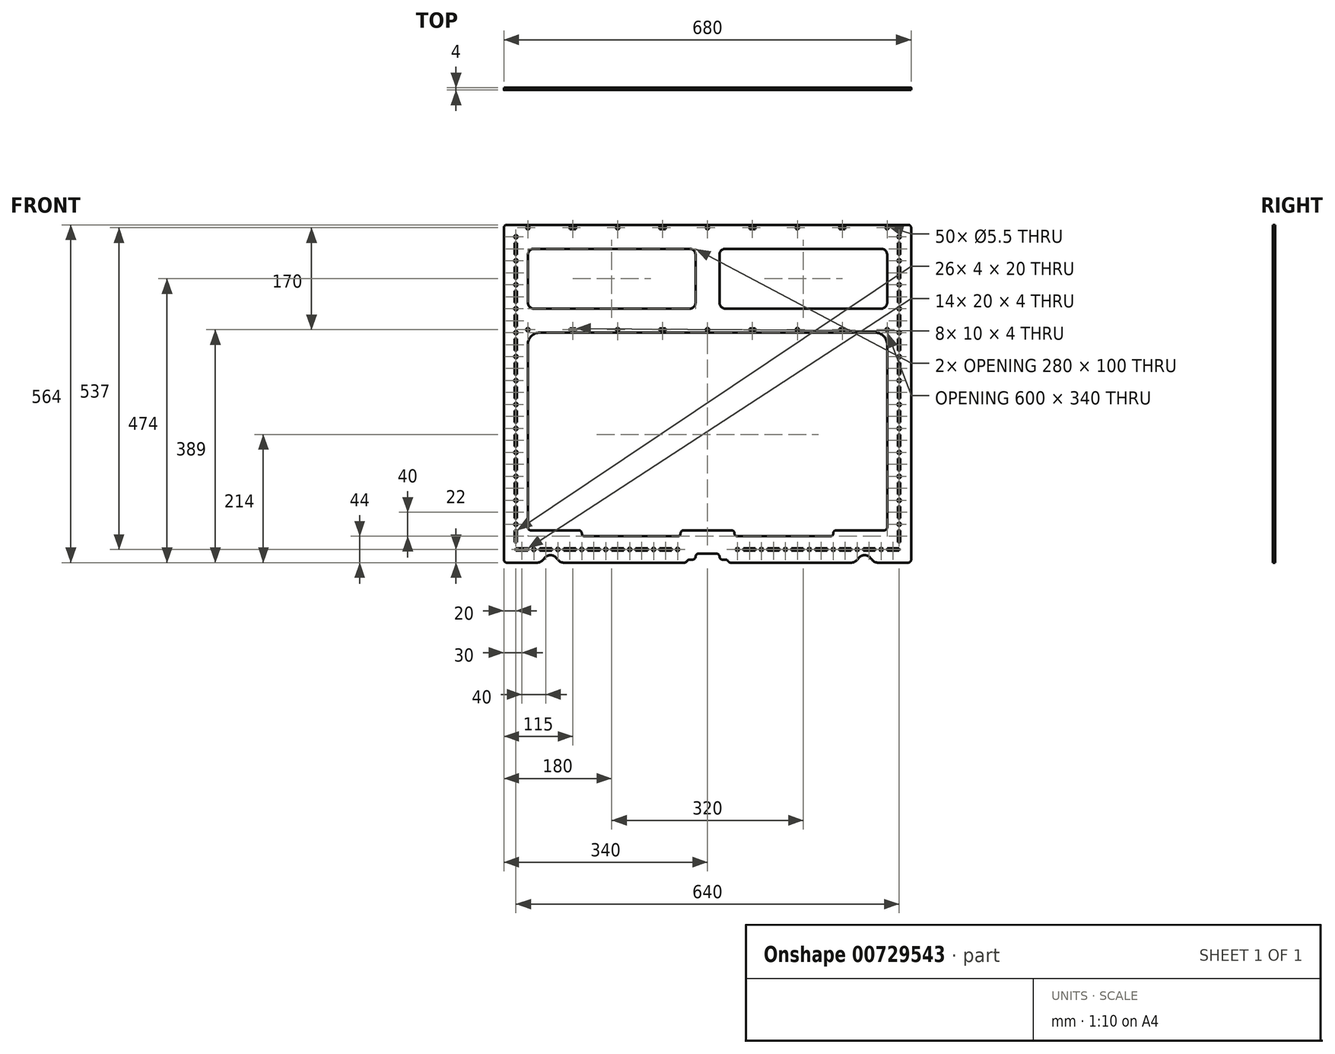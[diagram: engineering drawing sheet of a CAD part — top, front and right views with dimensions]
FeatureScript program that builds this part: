
annotation { "Feature Type Name" : "Feature", "Feature Type Description" : "" }
export const myFeature = defineFeature(function(context is Context, id is Id, definition is map)
    precondition{}
    {
        {
            var Q0;
            Q0=qCreatedBy(makeId("Front.planeOp"),FACE);
            var sketch = newSketch(context, id + "F0", { "sketchPlane" : qUnion([Q0])});
            skLineSegment(sketch, "E0.bottom", {"start": v(0, 0) * mm, "end": v(640, 0) * mm, "construction": true});
            skLineSegment(sketch, "E0.top", {"start": v(0, 365) * mm, "end": v(640, 365) * mm, "construction": true});
            skLineSegment(sketch, "E0.left", {"start": v(0, 0) * mm, "end": v(0, 540) * mm, "construction": true});
            skLineSegment(sketch, "E0.right", {"start": v(640, 0) * mm, "end": v(640, 540) * mm, "construction": true});
            skLineSegment(sketch, "E1.top", {"start": v(-15, -24) * mm, "end": v(34.7, -24) * mm});
            skLineSegment(sketch, "E2.bottom", {"start": v(40, 360) * mm, "end": v(600, 360) * mm});
            skLineSegment(sketch, "E2.top", {"start": v(115, 20) * mm, "end": v(270, 20) * mm});
            skLineSegment(sketch, "E2.left", {"start": v(20, 340) * mm, "end": v(20, 35) * mm});
            skLineSegment(sketch, "E2.right", {"start": v(620, 340) * mm, "end": v(620, 35) * mm});
            skLineSegment(sketch, "E3.top", {"start": v(-15, 540) * mm, "end": v(655, 540) * mm});
            skLineSegment(sketch, "E4.bottom", {"start": v(30, 500) * mm, "end": v(290, 500) * mm});
            skLineSegment(sketch, "E4.top", {"start": v(30, 400) * mm, "end": v(290, 400) * mm});
            skLineSegment(sketch, "E4.left", {"start": v(20, 490) * mm, "end": v(20, 410) * mm});
            skLineSegment(sketch, "E4.right", {"start": v(620, 490) * mm, "end": v(620, 410) * mm});
            skLineSegment(sketch, "E5", {"start": v(0, 535) * mm, "end": v(640, 535) * mm, "construction": true});
            skLineSegment(sketch, "E6", {"start": v(660, 535) * mm, "end": v(660, -19) * mm});
            skLineSegment(sketch, "E7", {"start": v(-20, 535) * mm, "end": v(-20, -19) * mm});
            skCircle(sketch, "E8", {"center": v(20, 535) * mm, "radius": 2.75 * mm});
            skLineSegment(sketch, "E9.bottom", {"start": v(0, 0) * mm, "end": v(20, 0) * mm});
            skLineSegment(sketch, "E9.top", {"start": v(0, -4) * mm, "end": v(20, -4) * mm});
            skLineSegment(sketch, "E9.left", {"start": v(0, 0) * mm, "end": v(0, -4) * mm});
            skLineSegment(sketch, "E9.right", {"start": v(20, 0) * mm, "end": v(20, -4) * mm});
            skLineSegment(sketch, "E10.bottom", {"start": v(2, 10) * mm, "end": v(-2, 10) * mm});
            skLineSegment(sketch, "E10.top", {"start": v(2, 30) * mm, "end": v(-2, 30) * mm});
            skLineSegment(sketch, "E10.left", {"start": v(2, 10) * mm, "end": v(2, 30) * mm});
            skLineSegment(sketch, "E10.right", {"start": v(-2, 10) * mm, "end": v(-2, 30) * mm});
            skPoint(sketch, "E10.middle", {"position": v(0, 20) * mm});
            skCircle(sketch, "E11.1.0.0", {"center": v(170, 535) * mm, "radius": 2.75 * mm});
            skCircle(sketch, "E11.2.0.0", {"center": v(320, 535) * mm, "radius": 2.75 * mm});
            skCircle(sketch, "E11.3.0.0", {"center": v(470, 535) * mm, "radius": 2.75 * mm});
            skCircle(sketch, "E11.4.0.0", {"center": v(620, 535) * mm, "radius": 2.75 * mm});
            skLineSegment(sketch, "E11.direction1", {"start": v(20, 535) * mm, "end": v(170, 535) * mm, "construction": true});
            skCircle(sketch, "E12", {"center": v(20, 365) * mm, "radius": 2.75 * mm});
            skCircle(sketch, "E13.1.0.0", {"center": v(170, 365) * mm, "radius": 2.75 * mm});
            skCircle(sketch, "E13.2.0.0", {"center": v(320, 365) * mm, "radius": 2.75 * mm});
            skCircle(sketch, "E13.3.0.0", {"center": v(470, 365) * mm, "radius": 2.75 * mm});
            skCircle(sketch, "E13.4.0.0", {"center": v(620, 365) * mm, "radius": 2.75 * mm});
            skLineSegment(sketch, "E13.direction1", {"start": v(20, 365) * mm, "end": v(170, 365) * mm, "construction": true});
            skCircle(sketch, "E14", {"center": v(0, 40) * mm, "radius": 2.75 * mm});
            skLineSegment(sketch, "E15.0.1.0", {"start": v(2, 50) * mm, "end": v(-2, 50) * mm});
            skLineSegment(sketch, "E15.0.1.1", {"start": v(-2, 50) * mm, "end": v(-2, 70) * mm});
            skLineSegment(sketch, "E15.0.1.2", {"start": v(2, 50) * mm, "end": v(2, 70) * mm});
            skLineSegment(sketch, "E15.0.1.3", {"start": v(2, 70) * mm, "end": v(-2, 70) * mm});
            skCircle(sketch, "E15.0.1.4", {"center": v(0, 80) * mm, "radius": 2.75 * mm});
            skLineSegment(sketch, "E15.0.2.0", {"start": v(2, 90) * mm, "end": v(-2, 90) * mm});
            skLineSegment(sketch, "E15.0.2.1", {"start": v(-2, 90) * mm, "end": v(-2, 110) * mm});
            skLineSegment(sketch, "E15.0.2.2", {"start": v(2, 90) * mm, "end": v(2, 110) * mm});
            skLineSegment(sketch, "E15.0.2.3", {"start": v(2, 110) * mm, "end": v(-2, 110) * mm});
            skCircle(sketch, "E15.0.2.4", {"center": v(0, 120) * mm, "radius": 2.75 * mm});
            skLineSegment(sketch, "E15.0.3.0", {"start": v(2, 130) * mm, "end": v(-2, 130) * mm});
            skLineSegment(sketch, "E15.0.3.1", {"start": v(-2, 130) * mm, "end": v(-2, 150) * mm});
            skLineSegment(sketch, "E15.0.3.2", {"start": v(2, 130) * mm, "end": v(2, 150) * mm});
            skLineSegment(sketch, "E15.0.3.3", {"start": v(2, 150) * mm, "end": v(-2, 150) * mm});
            skCircle(sketch, "E15.0.3.4", {"center": v(0, 160) * mm, "radius": 2.75 * mm});
            skLineSegment(sketch, "E15.0.4.0", {"start": v(2, 170) * mm, "end": v(-2, 170) * mm});
            skLineSegment(sketch, "E15.0.4.1", {"start": v(-2, 170) * mm, "end": v(-2, 190) * mm});
            skLineSegment(sketch, "E15.0.4.2", {"start": v(2, 170) * mm, "end": v(2, 190) * mm});
            skLineSegment(sketch, "E15.0.4.3", {"start": v(2, 190) * mm, "end": v(-2, 190) * mm});
            skCircle(sketch, "E15.0.4.4", {"center": v(0, 200) * mm, "radius": 2.75 * mm});
            skLineSegment(sketch, "E15.0.5.0", {"start": v(2, 210) * mm, "end": v(-2, 210) * mm});
            skLineSegment(sketch, "E15.0.5.1", {"start": v(-2, 210) * mm, "end": v(-2, 230) * mm});
            skLineSegment(sketch, "E15.0.5.2", {"start": v(2, 210) * mm, "end": v(2, 230) * mm});
            skLineSegment(sketch, "E15.0.5.3", {"start": v(2, 230) * mm, "end": v(-2, 230) * mm});
            skCircle(sketch, "E15.0.5.4", {"center": v(0, 240) * mm, "radius": 2.75 * mm});
            skLineSegment(sketch, "E15.0.6.0", {"start": v(2, 250) * mm, "end": v(-2, 250) * mm});
            skLineSegment(sketch, "E15.0.6.1", {"start": v(-2, 250) * mm, "end": v(-2, 270) * mm});
            skLineSegment(sketch, "E15.0.6.2", {"start": v(2, 250) * mm, "end": v(2, 270) * mm});
            skLineSegment(sketch, "E15.0.6.3", {"start": v(2, 270) * mm, "end": v(-2, 270) * mm});
            skCircle(sketch, "E15.0.6.4", {"center": v(0, 280) * mm, "radius": 2.75 * mm});
            skLineSegment(sketch, "E15.0.7.0", {"start": v(2, 290) * mm, "end": v(-2, 290) * mm});
            skLineSegment(sketch, "E15.0.7.1", {"start": v(-2, 290) * mm, "end": v(-2, 310) * mm});
            skLineSegment(sketch, "E15.0.7.2", {"start": v(2, 290) * mm, "end": v(2, 310) * mm});
            skLineSegment(sketch, "E15.0.7.3", {"start": v(2, 310) * mm, "end": v(-2, 310) * mm});
            skCircle(sketch, "E15.0.7.4", {"center": v(0, 320) * mm, "radius": 2.75 * mm});
            skLineSegment(sketch, "E15.0.8.0", {"start": v(2, 330) * mm, "end": v(-2, 330) * mm});
            skLineSegment(sketch, "E15.0.8.1", {"start": v(-2, 330) * mm, "end": v(-2, 350) * mm});
            skLineSegment(sketch, "E15.0.8.2", {"start": v(2, 330) * mm, "end": v(2, 350) * mm});
            skLineSegment(sketch, "E15.0.8.3", {"start": v(2, 350) * mm, "end": v(-2, 350) * mm});
            skCircle(sketch, "E15.0.8.4", {"center": v(0, 360) * mm, "radius": 2.75 * mm});
            skLineSegment(sketch, "E15.0.9.0", {"start": v(2, 370) * mm, "end": v(-2, 370) * mm});
            skLineSegment(sketch, "E15.0.9.1", {"start": v(-2, 370) * mm, "end": v(-2, 390) * mm});
            skLineSegment(sketch, "E15.0.9.2", {"start": v(2, 370) * mm, "end": v(2, 390) * mm});
            skLineSegment(sketch, "E15.0.9.3", {"start": v(2, 390) * mm, "end": v(-2, 390) * mm});
            skCircle(sketch, "E15.0.9.4", {"center": v(0, 400) * mm, "radius": 2.75 * mm});
            skLineSegment(sketch, "E15.0.10.0", {"start": v(2, 410) * mm, "end": v(-2, 410) * mm});
            skLineSegment(sketch, "E15.0.10.1", {"start": v(-2, 410) * mm, "end": v(-2, 430) * mm});
            skLineSegment(sketch, "E15.0.10.2", {"start": v(2, 410) * mm, "end": v(2, 430) * mm});
            skLineSegment(sketch, "E15.0.10.3", {"start": v(2, 430) * mm, "end": v(-2, 430) * mm});
            skCircle(sketch, "E15.0.10.4", {"center": v(0, 440) * mm, "radius": 2.75 * mm});
            skLineSegment(sketch, "E15.0.11.0", {"start": v(2, 450) * mm, "end": v(-2, 450) * mm});
            skLineSegment(sketch, "E15.0.11.1", {"start": v(-2, 450) * mm, "end": v(-2, 470) * mm});
            skLineSegment(sketch, "E15.0.11.2", {"start": v(2, 450) * mm, "end": v(2, 470) * mm});
            skLineSegment(sketch, "E15.0.11.3", {"start": v(2, 470) * mm, "end": v(-2, 470) * mm});
            skCircle(sketch, "E15.0.11.4", {"center": v(0, 480) * mm, "radius": 2.75 * mm});
            skLineSegment(sketch, "E15.0.12.0", {"start": v(2, 490) * mm, "end": v(-2, 490) * mm});
            skLineSegment(sketch, "E15.0.12.1", {"start": v(-2, 490) * mm, "end": v(-2, 510) * mm});
            skLineSegment(sketch, "E15.0.12.2", {"start": v(2, 490) * mm, "end": v(2, 510) * mm});
            skLineSegment(sketch, "E15.0.12.3", {"start": v(2, 510) * mm, "end": v(-2, 510) * mm});
            skCircle(sketch, "E15.0.12.4", {"center": v(0, 520) * mm, "radius": 2.75 * mm});
            skLineSegment(sketch, "E15.1.0.0", {"start": v(642, 10) * mm, "end": v(638, 10) * mm});
            skLineSegment(sketch, "E15.1.0.1", {"start": v(638, 10) * mm, "end": v(638, 30) * mm});
            skLineSegment(sketch, "E15.1.0.2", {"start": v(642, 10) * mm, "end": v(642, 30) * mm});
            skLineSegment(sketch, "E15.1.0.3", {"start": v(642, 30) * mm, "end": v(638, 30) * mm});
            skCircle(sketch, "E15.1.0.4", {"center": v(640, 40) * mm, "radius": 2.75 * mm});
            skLineSegment(sketch, "E15.1.1.0", {"start": v(642, 50) * mm, "end": v(638, 50) * mm});
            skLineSegment(sketch, "E15.1.1.1", {"start": v(638, 50) * mm, "end": v(638, 70) * mm});
            skLineSegment(sketch, "E15.1.1.2", {"start": v(642, 50) * mm, "end": v(642, 70) * mm});
            skLineSegment(sketch, "E15.1.1.3", {"start": v(642, 70) * mm, "end": v(638, 70) * mm});
            skCircle(sketch, "E15.1.1.4", {"center": v(640, 80) * mm, "radius": 2.75 * mm});
            skLineSegment(sketch, "E15.1.2.0", {"start": v(642, 90) * mm, "end": v(638, 90) * mm});
            skLineSegment(sketch, "E15.1.2.1", {"start": v(638, 90) * mm, "end": v(638, 110) * mm});
            skLineSegment(sketch, "E15.1.2.2", {"start": v(642, 90) * mm, "end": v(642, 110) * mm});
            skLineSegment(sketch, "E15.1.2.3", {"start": v(642, 110) * mm, "end": v(638, 110) * mm});
            skCircle(sketch, "E15.1.2.4", {"center": v(640, 120) * mm, "radius": 2.75 * mm});
            skLineSegment(sketch, "E15.1.3.0", {"start": v(642, 130) * mm, "end": v(638, 130) * mm});
            skLineSegment(sketch, "E15.1.3.1", {"start": v(638, 130) * mm, "end": v(638, 150) * mm});
            skLineSegment(sketch, "E15.1.3.2", {"start": v(642, 130) * mm, "end": v(642, 150) * mm});
            skLineSegment(sketch, "E15.1.3.3", {"start": v(642, 150) * mm, "end": v(638, 150) * mm});
            skCircle(sketch, "E15.1.3.4", {"center": v(640, 160) * mm, "radius": 2.75 * mm});
            skLineSegment(sketch, "E15.1.4.0", {"start": v(642, 170) * mm, "end": v(638, 170) * mm});
            skLineSegment(sketch, "E15.1.4.1", {"start": v(638, 170) * mm, "end": v(638, 190) * mm});
            skLineSegment(sketch, "E15.1.4.2", {"start": v(642, 170) * mm, "end": v(642, 190) * mm});
            skLineSegment(sketch, "E15.1.4.3", {"start": v(642, 190) * mm, "end": v(638, 190) * mm});
            skCircle(sketch, "E15.1.4.4", {"center": v(640, 200) * mm, "radius": 2.75 * mm});
            skLineSegment(sketch, "E15.1.5.0", {"start": v(642, 210) * mm, "end": v(638, 210) * mm});
            skLineSegment(sketch, "E15.1.5.1", {"start": v(638, 210) * mm, "end": v(638, 230) * mm});
            skLineSegment(sketch, "E15.1.5.2", {"start": v(642, 210) * mm, "end": v(642, 230) * mm});
            skLineSegment(sketch, "E15.1.5.3", {"start": v(642, 230) * mm, "end": v(638, 230) * mm});
            skCircle(sketch, "E15.1.5.4", {"center": v(640, 240) * mm, "radius": 2.75 * mm});
            skLineSegment(sketch, "E15.1.6.0", {"start": v(642, 250) * mm, "end": v(638, 250) * mm});
            skLineSegment(sketch, "E15.1.6.1", {"start": v(638, 250) * mm, "end": v(638, 270) * mm});
            skLineSegment(sketch, "E15.1.6.2", {"start": v(642, 250) * mm, "end": v(642, 270) * mm});
            skLineSegment(sketch, "E15.1.6.3", {"start": v(642, 270) * mm, "end": v(638, 270) * mm});
            skCircle(sketch, "E15.1.6.4", {"center": v(640, 280) * mm, "radius": 2.75 * mm});
            skLineSegment(sketch, "E15.1.7.0", {"start": v(642, 290) * mm, "end": v(638, 290) * mm});
            skLineSegment(sketch, "E15.1.7.1", {"start": v(638, 290) * mm, "end": v(638, 310) * mm});
            skLineSegment(sketch, "E15.1.7.2", {"start": v(642, 290) * mm, "end": v(642, 310) * mm});
            skLineSegment(sketch, "E15.1.7.3", {"start": v(642, 310) * mm, "end": v(638, 310) * mm});
            skCircle(sketch, "E15.1.7.4", {"center": v(640, 320) * mm, "radius": 2.75 * mm});
            skLineSegment(sketch, "E15.1.8.0", {"start": v(642, 330) * mm, "end": v(638, 330) * mm});
            skLineSegment(sketch, "E15.1.8.1", {"start": v(638, 330) * mm, "end": v(638, 350) * mm});
            skLineSegment(sketch, "E15.1.8.2", {"start": v(642, 330) * mm, "end": v(642, 350) * mm});
            skLineSegment(sketch, "E15.1.8.3", {"start": v(642, 350) * mm, "end": v(638, 350) * mm});
            skCircle(sketch, "E15.1.8.4", {"center": v(640, 360) * mm, "radius": 2.75 * mm});
            skLineSegment(sketch, "E15.1.9.0", {"start": v(642, 370) * mm, "end": v(638, 370) * mm});
            skLineSegment(sketch, "E15.1.9.1", {"start": v(638, 370) * mm, "end": v(638, 390) * mm});
            skLineSegment(sketch, "E15.1.9.2", {"start": v(642, 370) * mm, "end": v(642, 390) * mm});
            skLineSegment(sketch, "E15.1.9.3", {"start": v(642, 390) * mm, "end": v(638, 390) * mm});
            skCircle(sketch, "E15.1.9.4", {"center": v(640, 400) * mm, "radius": 2.75 * mm});
            skLineSegment(sketch, "E15.1.10.0", {"start": v(642, 410) * mm, "end": v(638, 410) * mm});
            skLineSegment(sketch, "E15.1.10.1", {"start": v(638, 410) * mm, "end": v(638, 430) * mm});
            skLineSegment(sketch, "E15.1.10.2", {"start": v(642, 410) * mm, "end": v(642, 430) * mm});
            skLineSegment(sketch, "E15.1.10.3", {"start": v(642, 430) * mm, "end": v(638, 430) * mm});
            skCircle(sketch, "E15.1.10.4", {"center": v(640, 440) * mm, "radius": 2.75 * mm});
            skLineSegment(sketch, "E15.1.11.0", {"start": v(642, 450) * mm, "end": v(638, 450) * mm});
            skLineSegment(sketch, "E15.1.11.1", {"start": v(638, 450) * mm, "end": v(638, 470) * mm});
            skLineSegment(sketch, "E15.1.11.2", {"start": v(642, 450) * mm, "end": v(642, 470) * mm});
            skLineSegment(sketch, "E15.1.11.3", {"start": v(642, 470) * mm, "end": v(638, 470) * mm});
            skCircle(sketch, "E15.1.11.4", {"center": v(640, 480) * mm, "radius": 2.75 * mm});
            skLineSegment(sketch, "E15.1.12.0", {"start": v(642, 490) * mm, "end": v(638, 490) * mm});
            skLineSegment(sketch, "E15.1.12.1", {"start": v(638, 490) * mm, "end": v(638, 510) * mm});
            skLineSegment(sketch, "E15.1.12.2", {"start": v(642, 490) * mm, "end": v(642, 510) * mm});
            skLineSegment(sketch, "E15.1.12.3", {"start": v(642, 510) * mm, "end": v(638, 510) * mm});
            skCircle(sketch, "E15.1.12.4", {"center": v(640, 520) * mm, "radius": 2.75 * mm});
            skLineSegment(sketch, "E15.direction1", {"start": v(-2, 10) * mm, "end": v(638, 10) * mm, "construction": true});
            skLineSegment(sketch, "E15.direction2", {"start": v(-2, 10) * mm, "end": v(-2, 50) * mm, "construction": true});
            skCircle(sketch, "E16", {"center": v(30, -2) * mm, "radius": 2.75 * mm});
            skLineSegment(sketch, "E17.1.0.0", {"start": v(40, 0) * mm, "end": v(40, -4) * mm});
            skLineSegment(sketch, "E17.1.0.1", {"start": v(40, 0) * mm, "end": v(60, 0) * mm});
            skLineSegment(sketch, "E17.1.0.2", {"start": v(40, -4) * mm, "end": v(60, -4) * mm});
            skLineSegment(sketch, "E17.1.0.3", {"start": v(60, 0) * mm, "end": v(60, -4) * mm});
            skCircle(sketch, "E17.1.0.4", {"center": v(70, -2) * mm, "radius": 2.75 * mm});
            skLineSegment(sketch, "E17.2.0.0", {"start": v(80, 0) * mm, "end": v(80, -4) * mm});
            skLineSegment(sketch, "E17.2.0.1", {"start": v(80, 0) * mm, "end": v(100, 0) * mm});
            skLineSegment(sketch, "E17.2.0.2", {"start": v(80, -4) * mm, "end": v(100, -4) * mm});
            skLineSegment(sketch, "E17.2.0.3", {"start": v(100, 0) * mm, "end": v(100, -4) * mm});
            skCircle(sketch, "E17.2.0.4", {"center": v(110, -2) * mm, "radius": 2.75 * mm});
            skLineSegment(sketch, "E17.3.0.0", {"start": v(120, 0) * mm, "end": v(120, -4) * mm});
            skLineSegment(sketch, "E17.3.0.1", {"start": v(120, 0) * mm, "end": v(140, 0) * mm});
            skLineSegment(sketch, "E17.3.0.2", {"start": v(120, -4) * mm, "end": v(140, -4) * mm});
            skLineSegment(sketch, "E17.3.0.3", {"start": v(140, 0) * mm, "end": v(140, -4) * mm});
            skCircle(sketch, "E17.3.0.4", {"center": v(150, -2) * mm, "radius": 2.75 * mm});
            skLineSegment(sketch, "E17.4.0.0", {"start": v(160, 0) * mm, "end": v(160, -4) * mm});
            skLineSegment(sketch, "E17.4.0.1", {"start": v(160, 0) * mm, "end": v(180, 0) * mm});
            skLineSegment(sketch, "E17.4.0.2", {"start": v(160, -4) * mm, "end": v(180, -4) * mm});
            skLineSegment(sketch, "E17.4.0.3", {"start": v(180, 0) * mm, "end": v(180, -4) * mm});
            skCircle(sketch, "E17.4.0.4", {"center": v(190, -2) * mm, "radius": 2.75 * mm});
            skLineSegment(sketch, "E17.5.0.0", {"start": v(200, 0) * mm, "end": v(200, -4) * mm});
            skLineSegment(sketch, "E17.5.0.1", {"start": v(200, 0) * mm, "end": v(220, 0) * mm});
            skLineSegment(sketch, "E17.5.0.2", {"start": v(200, -4) * mm, "end": v(220, -4) * mm});
            skLineSegment(sketch, "E17.5.0.3", {"start": v(220, 0) * mm, "end": v(220, -4) * mm});
            skCircle(sketch, "E17.5.0.4", {"center": v(230, -2) * mm, "radius": 2.75 * mm});
            skLineSegment(sketch, "E17.6.0.0", {"start": v(240, 0) * mm, "end": v(240, -4) * mm});
            skLineSegment(sketch, "E17.6.0.1", {"start": v(240, 0) * mm, "end": v(260, 0) * mm});
            skLineSegment(sketch, "E17.6.0.2", {"start": v(240, -4) * mm, "end": v(260, -4) * mm});
            skLineSegment(sketch, "E17.6.0.3", {"start": v(260, 0) * mm, "end": v(260, -4) * mm});
            skCircle(sketch, "E17.6.0.4", {"center": v(270, -2) * mm, "radius": 2.75 * mm});
            skLineSegment(sketch, "E17.direction1", {"start": v(0, -4) * mm, "end": v(40, -4) * mm, "construction": true});
            skLineSegment(sketch, "E18", {"start": v(320, -24) * mm, "end": v(320, 48.13) * mm, "construction": true});
            skLineSegment(sketch, "E19.MirrorCS", {"start": v(640, 0) * mm, "end": v(640, -4) * mm});
            skLineSegment(sketch, "E20.MirrorCS", {"start": v(480, 0) * mm, "end": v(480, -4) * mm});
            skLineSegment(sketch, "E21.MirrorCS", {"start": v(440, 0) * mm, "end": v(440, -4) * mm});
            skLineSegment(sketch, "E22.MirrorCS", {"start": v(580, 0) * mm, "end": v(580, -4) * mm});
            skLineSegment(sketch, "E23.MirrorCS", {"start": v(500, 0) * mm, "end": v(500, -4) * mm});
            skLineSegment(sketch, "E24.MirrorCS", {"start": v(560, 0) * mm, "end": v(560, -4) * mm});
            skLineSegment(sketch, "E25.MirrorCS", {"start": v(540, 0) * mm, "end": v(540, -4) * mm});
            skLineSegment(sketch, "E26.MirrorCS", {"start": v(380, 0) * mm, "end": v(380, -4) * mm});
            skLineSegment(sketch, "E27.MirrorCS", {"start": v(460, 0) * mm, "end": v(460, -4) * mm});
            skLineSegment(sketch, "E28.MirrorCS", {"start": v(600, 0) * mm, "end": v(600, -4) * mm});
            skLineSegment(sketch, "E29.MirrorCS", {"start": v(400, 0) * mm, "end": v(400, -4) * mm});
            skLineSegment(sketch, "E30.MirrorCS", {"start": v(520, 0) * mm, "end": v(520, -4) * mm});
            skLineSegment(sketch, "E31.MirrorCS", {"start": v(420, 0) * mm, "end": v(420, -4) * mm});
            skLineSegment(sketch, "E32.MirrorCS", {"start": v(620, 0) * mm, "end": v(620, -4) * mm});
            skLineSegment(sketch, "E33.MirrorCS", {"start": v(640, -4) * mm, "end": v(620, -4) * mm});
            skLineSegment(sketch, "E34.MirrorCS", {"start": v(600, 0) * mm, "end": v(580, 0) * mm});
            skLineSegment(sketch, "E35.MirrorCS", {"start": v(640, 0) * mm, "end": v(620, 0) * mm});
            skLineSegment(sketch, "E36.MirrorCS", {"start": v(440, 0) * mm, "end": v(420, 0) * mm});
            skLineSegment(sketch, "E37.MirrorCS", {"start": v(560, 0) * mm, "end": v(540, 0) * mm});
            skLineSegment(sketch, "E38.MirrorCS", {"start": v(520, 0) * mm, "end": v(500, 0) * mm});
            skLineSegment(sketch, "E39.MirrorCS", {"start": v(480, 0) * mm, "end": v(460, 0) * mm});
            skLineSegment(sketch, "E40.MirrorCS", {"start": v(400, 0) * mm, "end": v(380, 0) * mm});
            skCircle(sketch, "E41.MirrorC", {"center": v(570, -2) * mm, "radius": 2.75 * mm});
            skCircle(sketch, "E42.MirrorC", {"center": v(610, -2) * mm, "radius": 2.75 * mm});
            skLineSegment(sketch, "E43.MirrorCS", {"start": v(600, -4) * mm, "end": v(580, -4) * mm});
            skLineSegment(sketch, "E44.MirrorCS", {"start": v(520, -4) * mm, "end": v(500, -4) * mm});
            skLineSegment(sketch, "E45.MirrorCS", {"start": v(560, -4) * mm, "end": v(540, -4) * mm});
            skCircle(sketch, "E46.MirrorC", {"center": v(450, -2) * mm, "radius": 2.75 * mm});
            skCircle(sketch, "E47.MirrorC", {"center": v(530, -2) * mm, "radius": 2.75 * mm});
            skLineSegment(sketch, "E48.MirrorCS", {"start": v(440, -4) * mm, "end": v(420, -4) * mm});
            skCircle(sketch, "E49.MirrorC", {"center": v(370, -2) * mm, "radius": 2.75 * mm});
            skCircle(sketch, "E50.MirrorC", {"center": v(410, -2) * mm, "radius": 2.75 * mm});
            skCircle(sketch, "E51.MirrorC", {"center": v(490, -2) * mm, "radius": 2.75 * mm});
            skLineSegment(sketch, "E52.MirrorCS", {"start": v(400, -4) * mm, "end": v(380, -4) * mm});
            skLineSegment(sketch, "E53.MirrorCS", {"start": v(480, -4) * mm, "end": v(460, -4) * mm});
            skLineSegment(sketch, "E54.top", {"start": v(25, 30) * mm, "end": v(105, 30) * mm});
            skLineSegment(sketch, "E54.right", {"start": v(110, 25) * mm, "end": v(110, 25) * mm});
            skLineSegment(sketch, "E55.MirrorCS", {"start": v(530, 25) * mm, "end": v(530, 25) * mm});
            skLineSegment(sketch, "E56.MirrorCS", {"start": v(615, 30) * mm, "end": v(535, 30) * mm});
            skPoint(sketch, "E57.orphan", {"position": v(320, 20) * mm});
            skLineSegment(sketch, "E58", {"start": v(300, -19) * mm, "end": v(300, -19) * mm});
            skLineSegment(sketch, "E59", {"start": v(305, -9) * mm, "end": v(320, -9) * mm});
            skLineSegment(sketch, "E60.MirrorCS", {"start": v(340, -9) * mm, "end": v(320, -9) * mm});
            skLineSegment(sketch, "E61.MirrorCS", {"start": v(340, -19) * mm, "end": v(340, -19) * mm});
            skArc(sketch, "E62", {"start": v(68.23, -17.18) * mm, "mid": v(57.75, -11.5) * mm, "end": v(47.27, -17.18) * mm});
            skArc(sketch, "E63.MirrorC", {"start": v(571.77, -17.18) * mm, "mid": v(582.25, -11.5) * mm, "end": v(592.73, -17.18) * mm});
            skPoint(sketch, "E64.visualSharp", {"position": v(300, -9) * mm});
            skPoint(sketch, "E65.visualSharp", {"position": v(340, -9) * mm});
            skLineSegment(sketch, "E66.trimOffspring", {"start": v(360, -24) * mm, "end": v(559.2, -24) * mm});
            skPoint(sketch, "E67.visualSharp", {"position": v(300, -24) * mm});
            skPoint(sketch, "E68.visualSharp", {"position": v(340, -24) * mm});
            skLineSegment(sketch, "E69.trimOffspring", {"start": v(80.8, -24) * mm, "end": v(281.34, -24) * mm});
            skLineSegment(sketch, "E70.trimOffspring", {"start": v(605.3, -24) * mm, "end": v(655, -24) * mm});
            skPoint(sketch, "E71.visualSharp", {"position": v(45.25, -24) * mm});
            skArc(sketch, "E71.filletArc", {"start": v(34.7, -24) * mm, "mid": v(41.85, -22.19) * mm, "end": v(47.27, -17.18) * mm});
            skPoint(sketch, "E72.visualSharp", {"position": v(70.25, -24) * mm});
            skArc(sketch, "E72.filletArc", {"start": v(68.23, -17.18) * mm, "mid": v(73.65, -22.19) * mm, "end": v(80.8, -24) * mm});
            skPoint(sketch, "E73.visualSharp", {"position": v(569.75, -24) * mm});
            skArc(sketch, "E73.filletArc", {"start": v(559.2, -24) * mm, "mid": v(566.35, -22.19) * mm, "end": v(571.77, -17.18) * mm});
            skPoint(sketch, "E74.visualSharp", {"position": v(594.75, -24) * mm});
            skArc(sketch, "E74.filletArc", {"start": v(592.73, -17.18) * mm, "mid": v(598.15, -22.19) * mm, "end": v(605.3, -24) * mm});
            skPoint(sketch, "E75.orphan", {"position": v(620, 20) * mm});
            skPoint(sketch, "E54.left.start.orphan", {"position": v(20, 20) * mm});
            skPoint(sketch, "E76.visualSharp", {"position": v(20, 30) * mm});
            skArc(sketch, "E76.filletArc", {"start": v(20, 35) * mm, "mid": v(21.46, 31.46) * mm, "end": v(25, 30) * mm});
            skPoint(sketch, "E77.visualSharp", {"position": v(110, 30) * mm});
            skArc(sketch, "E77.filletArc", {"start": v(110, 25) * mm, "mid": v(108.54, 28.54) * mm, "end": v(105, 30) * mm});
            skPoint(sketch, "E78.visualSharp", {"position": v(110, 20) * mm});
            skArc(sketch, "E78.filletArc", {"start": v(110, 25) * mm, "mid": v(111.46, 21.46) * mm, "end": v(115, 20) * mm});
            skPoint(sketch, "E79.visualSharp", {"position": v(530, 20) * mm});
            skArc(sketch, "E79.filletArc", {"start": v(525, 20) * mm, "mid": v(528.54, 21.46) * mm, "end": v(530, 25) * mm});
            skPoint(sketch, "E80.visualSharp", {"position": v(530, 30) * mm});
            skArc(sketch, "E80.filletArc", {"start": v(535, 30) * mm, "mid": v(531.46, 28.54) * mm, "end": v(530, 25) * mm});
            skPoint(sketch, "E81.visualSharp", {"position": v(620, 30) * mm});
            skArc(sketch, "E81.filletArc", {"start": v(615, 30) * mm, "mid": v(618.54, 31.46) * mm, "end": v(620, 35) * mm});
            skPoint(sketch, "E82.visualSharp", {"position": v(660, 540) * mm});
            skArc(sketch, "E82.filletArc", {"start": v(660, 535) * mm, "mid": v(658.54, 538.54) * mm, "end": v(655, 540) * mm});
            skPoint(sketch, "E83.visualSharp", {"position": v(-20, 540) * mm});
            skArc(sketch, "E83.filletArc", {"start": v(-15, 540) * mm, "mid": v(-18.54, 538.54) * mm, "end": v(-20, 535) * mm});
            skPoint(sketch, "E84.visualSharp", {"position": v(-20, -24) * mm});
            skArc(sketch, "E84.filletArc", {"start": v(-20, -19) * mm, "mid": v(-18.54, -22.54) * mm, "end": v(-15, -24) * mm});
            skPoint(sketch, "E85.visualSharp", {"position": v(660, -24) * mm});
            skArc(sketch, "E85.filletArc", {"start": v(655, -24) * mm, "mid": v(658.54, -22.54) * mm, "end": v(660, -19) * mm});
            skLineSegment(sketch, "E86.top", {"start": v(360, 30) * mm, "end": v(280, 30) * mm});
            skLineSegment(sketch, "E86.left", {"start": v(365, 25) * mm, "end": v(365, 25) * mm});
            skLineSegment(sketch, "E86.right", {"start": v(275, 25) * mm, "end": v(275, 25) * mm});
            skPoint(sketch, "E86.middle", {"position": v(320, 25) * mm});
            skLineSegment(sketch, "E87.trimOffspring", {"start": v(370, 20) * mm, "end": v(525, 20) * mm});
            skPoint(sketch, "E88.visualSharp", {"position": v(275, 20) * mm});
            skArc(sketch, "E88.filletArc", {"start": v(270, 20) * mm, "mid": v(273.54, 21.46) * mm, "end": v(275, 25) * mm});
            skPoint(sketch, "E89.visualSharp", {"position": v(275, 30) * mm});
            skArc(sketch, "E89.filletArc", {"start": v(280, 30) * mm, "mid": v(276.46, 28.54) * mm, "end": v(275, 25) * mm});
            skPoint(sketch, "E90.visualSharp", {"position": v(365, 30) * mm});
            skArc(sketch, "E90.filletArc", {"start": v(365, 25) * mm, "mid": v(363.54, 28.54) * mm, "end": v(360, 30) * mm});
            skPoint(sketch, "E91.visualSharp", {"position": v(365, 20) * mm});
            skArc(sketch, "E91.filletArc", {"start": v(365, 25) * mm, "mid": v(366.46, 21.46) * mm, "end": v(370, 20) * mm});
            skLineSegment(sketch, "E92.bottom", {"start": v(90, 537) * mm, "end": v(100, 537) * mm});
            skLineSegment(sketch, "E92.top", {"start": v(90, 533) * mm, "end": v(100, 533) * mm});
            skLineSegment(sketch, "E92.left", {"start": v(90, 537) * mm, "end": v(90, 533) * mm});
            skLineSegment(sketch, "E92.right", {"start": v(100, 537) * mm, "end": v(100, 533) * mm});
            skPoint(sketch, "E92.middle", {"position": v(95, 535) * mm});
            skLineSegment(sketch, "E93.0.1.0", {"start": v(90, 367) * mm, "end": v(100, 367) * mm});
            skLineSegment(sketch, "E93.0.1.1", {"start": v(90, 367) * mm, "end": v(90, 363) * mm});
            skLineSegment(sketch, "E93.0.1.2", {"start": v(90, 363) * mm, "end": v(100, 363) * mm});
            skLineSegment(sketch, "E93.0.1.3", {"start": v(100, 367) * mm, "end": v(100, 363) * mm});
            skLineSegment(sketch, "E93.1.0.0", {"start": v(240, 537) * mm, "end": v(250, 537) * mm});
            skLineSegment(sketch, "E93.1.0.1", {"start": v(240, 537) * mm, "end": v(240, 533) * mm});
            skLineSegment(sketch, "E93.1.0.2", {"start": v(240, 533) * mm, "end": v(250, 533) * mm});
            skLineSegment(sketch, "E93.1.0.3", {"start": v(250, 537) * mm, "end": v(250, 533) * mm});
            skLineSegment(sketch, "E93.1.1.0", {"start": v(240, 367) * mm, "end": v(250, 367) * mm});
            skLineSegment(sketch, "E93.1.1.1", {"start": v(240, 367) * mm, "end": v(240, 363) * mm});
            skLineSegment(sketch, "E93.1.1.2", {"start": v(240, 363) * mm, "end": v(250, 363) * mm});
            skLineSegment(sketch, "E93.1.1.3", {"start": v(250, 367) * mm, "end": v(250, 363) * mm});
            skLineSegment(sketch, "E93.2.0.0", {"start": v(390, 537) * mm, "end": v(400, 537) * mm});
            skLineSegment(sketch, "E93.2.0.1", {"start": v(390, 537) * mm, "end": v(390, 533) * mm});
            skLineSegment(sketch, "E93.2.0.2", {"start": v(390, 533) * mm, "end": v(400, 533) * mm});
            skLineSegment(sketch, "E93.2.0.3", {"start": v(400, 537) * mm, "end": v(400, 533) * mm});
            skLineSegment(sketch, "E93.2.1.0", {"start": v(390, 367) * mm, "end": v(400, 367) * mm});
            skLineSegment(sketch, "E93.2.1.1", {"start": v(390, 367) * mm, "end": v(390, 363) * mm});
            skLineSegment(sketch, "E93.2.1.2", {"start": v(390, 363) * mm, "end": v(400, 363) * mm});
            skLineSegment(sketch, "E93.2.1.3", {"start": v(400, 367) * mm, "end": v(400, 363) * mm});
            skLineSegment(sketch, "E93.3.0.0", {"start": v(540, 537) * mm, "end": v(550, 537) * mm});
            skLineSegment(sketch, "E93.3.0.1", {"start": v(540, 537) * mm, "end": v(540, 533) * mm});
            skLineSegment(sketch, "E93.3.0.2", {"start": v(540, 533) * mm, "end": v(550, 533) * mm});
            skLineSegment(sketch, "E93.3.0.3", {"start": v(550, 537) * mm, "end": v(550, 533) * mm});
            skLineSegment(sketch, "E93.3.1.0", {"start": v(540, 367) * mm, "end": v(550, 367) * mm});
            skLineSegment(sketch, "E93.3.1.1", {"start": v(540, 367) * mm, "end": v(540, 363) * mm});
            skLineSegment(sketch, "E93.3.1.2", {"start": v(540, 363) * mm, "end": v(550, 363) * mm});
            skLineSegment(sketch, "E93.3.1.3", {"start": v(550, 367) * mm, "end": v(550, 363) * mm});
            skLineSegment(sketch, "E93.direction1", {"start": v(90, 533) * mm, "end": v(240, 533) * mm, "construction": true});
            skLineSegment(sketch, "E93.direction2", {"start": v(90, 533) * mm, "end": v(90, 363) * mm, "construction": true});
            skLineSegment(sketch, "E94", {"start": v(300, -14) * mm, "end": v(300, -14) * mm});
            skLineSegment(sketch, "E95", {"start": v(295, -19) * mm, "end": v(290, -19) * mm});
            skLineSegment(sketch, "E96", {"start": v(285, -24) * mm, "end": v(285, -24) * mm});
            skArc(sketch, "E97.filletArc", {"start": v(305, -9) * mm, "mid": v(301.46, -10.46) * mm, "end": v(300, -14) * mm});
            skPoint(sketch, "E98.visualSharp", {"position": v(285, -19) * mm});
            skArc(sketch, "E98.filletArc", {"start": v(290, -19) * mm, "mid": v(287.5, -19.67) * mm, "end": v(285.67, -21.5) * mm});
            skPoint(sketch, "E99.visualSharp", {"position": v(300, -19) * mm});
            skArc(sketch, "E99.filletArc", {"start": v(295, -19) * mm, "mid": v(298.54, -17.54) * mm, "end": v(300, -14) * mm});
            skArc(sketch, "E100.MirrorCS", {"start": v(335, -9) * mm, "mid": v(338.54, -10.46) * mm, "end": v(340, -14) * mm});
            skArc(sketch, "E101.MirrorCS", {"start": v(345, -19) * mm, "mid": v(341.46, -17.54) * mm, "end": v(340, -14) * mm});
            skLineSegment(sketch, "E102.MirrorCS", {"start": v(345, -19) * mm, "end": v(350, -19) * mm});
            skArc(sketch, "E103.MirrorCS", {"start": v(350, -19) * mm, "mid": v(352.5, -19.67) * mm, "end": v(354.33, -21.5) * mm});
            skLineSegment(sketch, "E104", {"start": v(360, -24) * mm, "end": v(358.66, -24) * mm});
            skPoint(sketch, "E105.visualSharp", {"position": v(285, -24) * mm});
            skArc(sketch, "E105.filletArc", {"start": v(281.34, -24) * mm, "mid": v(283.84, -23.33) * mm, "end": v(285.67, -21.5) * mm});
            skPoint(sketch, "E106.visualSharp", {"position": v(355, -24) * mm});
            skArc(sketch, "E106.filletArc", {"start": v(354.33, -21.5) * mm, "mid": v(356.16, -23.33) * mm, "end": v(358.66, -24) * mm});
            skPoint(sketch, "E107.visualSharp", {"position": v(620, 360) * mm});
            skArc(sketch, "E107.filletArc", {"start": v(620, 340) * mm, "mid": v(614.14, 354.14) * mm, "end": v(600, 360) * mm});
            skPoint(sketch, "E108.visualSharp", {"position": v(20, 360) * mm});
            skArc(sketch, "E108.filletArc", {"start": v(40, 360) * mm, "mid": v(25.86, 354.14) * mm, "end": v(20, 340) * mm});
            skPoint(sketch, "E109.visualSharp", {"position": v(20, 500) * mm});
            skArc(sketch, "E109.filletArc", {"start": v(30, 500) * mm, "mid": v(22.93, 497.07) * mm, "end": v(20, 490) * mm});
            skPoint(sketch, "E110.visualSharp", {"position": v(20, 400) * mm});
            skArc(sketch, "E110.filletArc", {"start": v(20, 410) * mm, "mid": v(22.93, 402.93) * mm, "end": v(30, 400) * mm});
            skPoint(sketch, "E111.visualSharp", {"position": v(620, 400) * mm});
            skArc(sketch, "E111.filletArc", {"start": v(610, 400) * mm, "mid": v(617.07, 402.93) * mm, "end": v(620, 410) * mm});
            skPoint(sketch, "E112.visualSharp", {"position": v(620, 500) * mm});
            skArc(sketch, "E112.filletArc", {"start": v(620, 490) * mm, "mid": v(617.07, 497.07) * mm, "end": v(610, 500) * mm});
            skLineSegment(sketch, "E113.0.left", {"start": v(340, 490) * mm, "end": v(340, 410) * mm});
            skLineSegment(sketch, "E113.0.right", {"start": v(300, 490) * mm, "end": v(300, 410) * mm});
            skPoint(sketch, "E114.end.orphan", {"position": v(320, 400) * mm});
            skPoint(sketch, "E114.start.orphan", {"position": v(320, 500) * mm});
            skLineSegment(sketch, "E115.trimOffspring", {"start": v(350, 500) * mm, "end": v(610, 500) * mm});
            skLineSegment(sketch, "E116.trimOffspring", {"start": v(350, 400) * mm, "end": v(610, 400) * mm});
            skPoint(sketch, "E117.visualSharp", {"position": v(340, 500) * mm});
            skArc(sketch, "E117.filletArc", {"start": v(350, 500) * mm, "mid": v(342.93, 497.07) * mm, "end": v(340, 490) * mm});
            skPoint(sketch, "E118.visualSharp", {"position": v(340, 400) * mm});
            skArc(sketch, "E118.filletArc", {"start": v(340, 410) * mm, "mid": v(342.93, 402.93) * mm, "end": v(350, 400) * mm});
            skPoint(sketch, "E119.visualSharp", {"position": v(300, 500) * mm});
            skArc(sketch, "E119.filletArc", {"start": v(300, 490) * mm, "mid": v(297.07, 497.07) * mm, "end": v(290, 500) * mm});
            skPoint(sketch, "E120.visualSharp", {"position": v(300, 400) * mm});
            skArc(sketch, "E120.filletArc", {"start": v(290, 400) * mm, "mid": v(297.07, 402.93) * mm, "end": v(300, 410) * mm});
            skSolve(sketch);
        }
        {
            var Q0;
            Q0=makeQuery(id+"F0.imprint","IMPRINT",FACE,{"disambiguationData":[TD([[makeQuery(id+"F0.imprint","IMPRINT",EDGE,{"derivedFrom":sQuery(id+"F0.wireOp",EDGE,"E1.top")}),1.0]])]});
            extrude(context, id + "F1", {"entities" : qUnion([Q0]), "depth" : 4 * mm, "offsetDistance" : 25 * mm});
        }
    });
